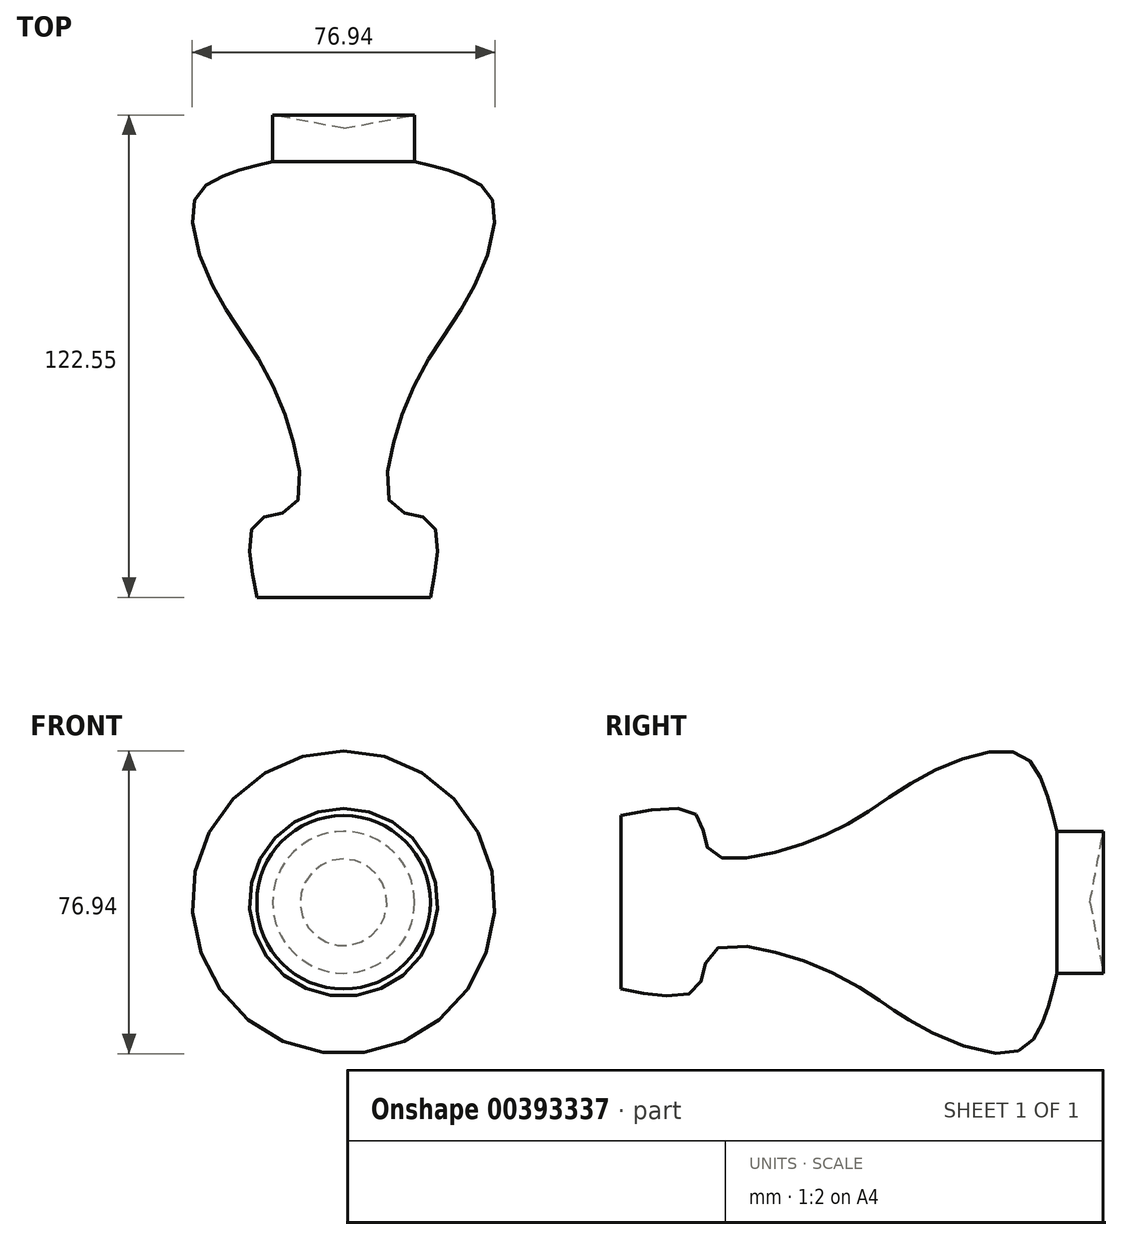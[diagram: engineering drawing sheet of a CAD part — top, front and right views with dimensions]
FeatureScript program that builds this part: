
annotation { "Feature Type Name" : "Feature", "Feature Type Description" : "" }
export const myFeature = defineFeature(function(context is Context, id is Id, definition is map)
    precondition{}
    {
        {
            var Q0;
            Q0=qCreatedBy(makeId("Top.planeOp"),FACE);
            var sketch = newSketch(context, id + "F0", { "sketchPlane" : qUnion([Q0])});
            skLineSegment(sketch, "E0", {"start": v(0, 77.25) * mm, "end": v(0, -114.57) * mm});
            skLineSegment(sketch, "E1", {"start": v(0, -66.25) * mm, "end": v(-22.04, -66.25) * mm});
            skFitSpline(sketch, "E2", {"points": [v(-22.04, -66.25) * mm, v(-22.04, -46.9) * mm, v(-12.69, -43.36) * mm, v(-13.69, -23.46) * mm, v(-22.04, -5.05) * mm, v(-33.48, 13.43) * mm, v(-37.81, 34.68) * mm, v(-28.72, 41.56) * mm, v(-18.02, 44.47) * mm], "startDerivative": vector(-35.62, 183.31) * mm, "endDerivative": vector(102.88, 23.59) * mm});
            skLineSegment(sketch, "E3", {"start": v(-18.02, 44.47) * mm, "end": v(-18.02, 56.3) * mm});
            skLineSegment(sketch, "E4", {"start": v(-18.02, 56.3) * mm, "end": v(0, 52.9) * mm});
            skSolve(sketch);
        }
        {
            var Q0;
            {var subQ0=sQuery(id+"F0.wireOp",EDGE,"E1");Q0=makeQuery(id+"F0.imprint","IMPRINT",FACE,{"disambiguationData":[TD([[makeQuery(id+"F0.imprint","IMPRINT",EDGE,{"derivedFrom":subQ0}),-1.0]])]});}
            var Q1;
            Q1=sQuery(id+"F0.wireOp",EDGE,"E0");
            revolve(context, id + "F1", {"entities" : qUnion([Q0]), "axis" : qUnion([Q1]), "revolveType" : RevolveType.FULL});
        }
    });
